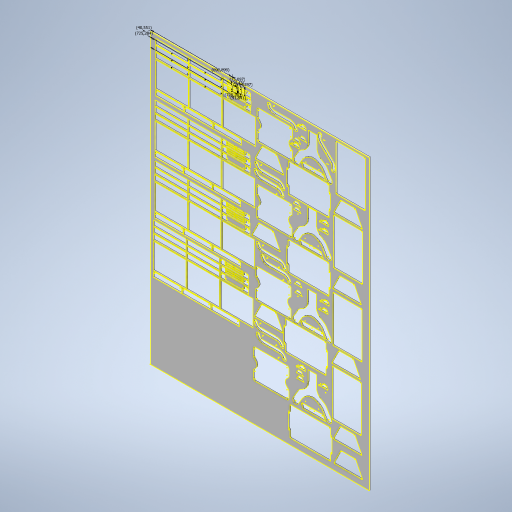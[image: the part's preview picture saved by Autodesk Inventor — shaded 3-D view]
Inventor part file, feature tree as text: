
AUTODESK INVENTOR PART (.ipt)
format: ipt  version: 2024 (Build 280153000, 153)  size: 3,642,880 bytes
history: native  units: mm
features: other x2, sketch x2, extrude x1, projected_geometry x1
ambient origin geometry x8: Origin, YZ Plane, XZ Plane, XY Plane, X Axis, Y Axis, Z Axis, Center Point
bodies: Body1 (feature_tree)
feature tree (6):
  other  "Sólido1"
  sketch  "Boceto1"  dims[d0=1850.0mm d1=2440.0mm]
  extrude  "Extrusión1"  Depth=2440.0mm
  sketch  "Boceto6"  dims[d2=10.0mm d3=0.0mm d52=94.43027mm d56=94.296686mm d60=690.898577mm d64=75.096659mm d65=725.283569mm d66=40.551099mm d67=728.282938mm d68=91.840811mm]
  other  "Visible"
  projected_geometry  "Contorno proyectado71"
